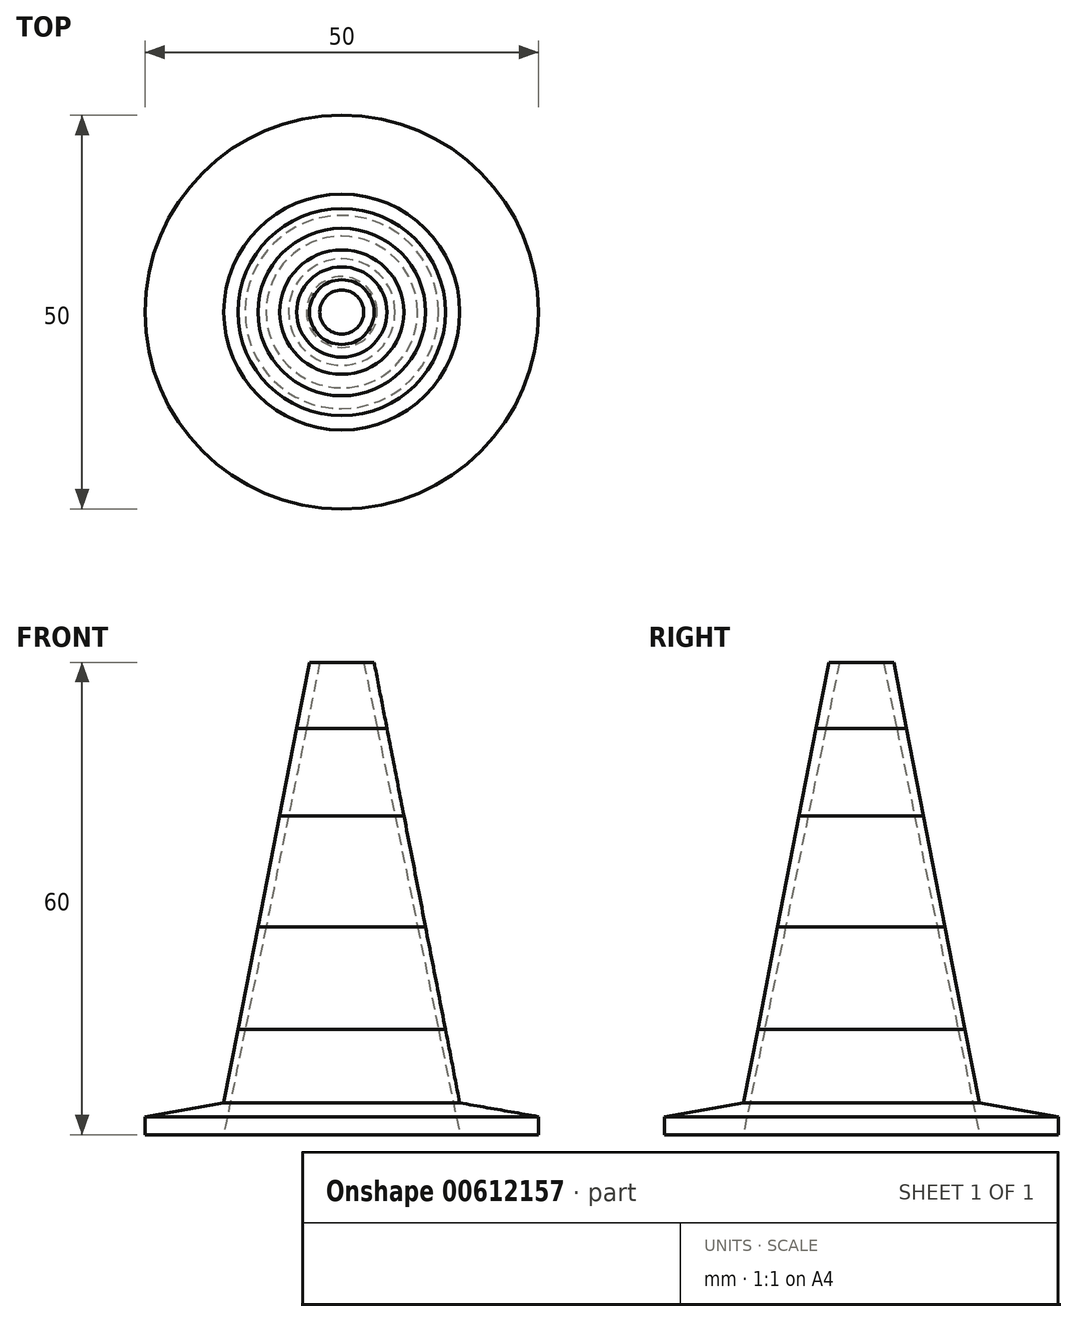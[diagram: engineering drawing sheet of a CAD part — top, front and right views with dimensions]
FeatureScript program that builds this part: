
annotation { "Feature Type Name" : "Feature", "Feature Type Description" : "" }
export const myFeature = defineFeature(function(context is Context, id is Id, definition is map)
    precondition{}
    {
        {
            var Q0;
            Q0=qCreatedBy(makeId("Front.planeOp"),FACE);
            var sketch = newSketch(context, id + "F0", { "sketchPlane" : qUnion([Q0])});
            skLineSegment(sketch, "E0", {"start": v(0, 0) * mm, "end": v(-25, 0) * mm});
            skLineSegment(sketch, "E1", {"start": v(-25, 0) * mm, "end": v(-25, 2.28) * mm});
            skLineSegment(sketch, "E2", {"start": v(-25, 2.28) * mm, "end": v(-14.98, 4.05) * mm});
            skLineSegment(sketch, "E3", {"start": v(-14.98, 4.05) * mm, "end": v(-4.1, 60) * mm});
            skLineSegment(sketch, "E4", {"start": v(-4.1, 60) * mm, "end": v(0, 60) * mm});
            skLineSegment(sketch, "E5", {"start": v(0, 60) * mm, "end": v(0, 0) * mm});
            skLineSegment(sketch, "E6", {"start": v(-13.17, 13.4) * mm, "end": v(0, 13.4) * mm});
            skLineSegment(sketch, "E7", {"start": v(-10.64, 26.4) * mm, "end": v(0, 26.4) * mm});
            skLineSegment(sketch, "E8", {"start": v(-7.9, 40.5) * mm, "end": v(0, 40.5) * mm});
            skLineSegment(sketch, "E9", {"start": v(-5.74, 51.6) * mm, "end": v(0, 51.6) * mm});
            skSolve(sketch);
        }
        {
            var Q0;
            {var subQ0=sQuery(id+"F0.wireOp",EDGE,"E4");Q0=makeQuery(id+"F0.imprint","IMPRINT",FACE,{"disambiguationData":[TD([[makeQuery(id+"F0.imprint","IMPRINT",EDGE,{"derivedFrom":subQ0}),-1.0]])]});}
            var Q1;
            Q1=sQuery(id+"F0.wireOp",EDGE,"E5");
            revolve(context, id + "F1", {"entities" : qUnion([Q0]), "axis" : qUnion([Q1]), "revolveType" : RevolveType.FULL});
        }
        {
            var Q0;
            {var subQ0=sQuery(id+"F0.wireOp",EDGE,"E8");Q0=makeQuery(id+"F0.imprint","IMPRINT",FACE,{"disambiguationData":[TD([[makeQuery(id+"F0.imprint","IMPRINT",EDGE,{"derivedFrom":subQ0}),1.0]])]});}
            var Q1;
            Q1=sQuery(id+"F0.wireOp",EDGE,"E5");
            revolve(context, id + "F2", {"entities" : qUnion([Q0]), "axis" : qUnion([Q1]), "revolveType" : RevolveType.FULL});
        }
        {
            var Q0;
            {var subQ0=sQuery(id+"F0.wireOp",EDGE,"E7");Q0=makeQuery(id+"F0.imprint","IMPRINT",FACE,{"disambiguationData":[TD([[makeQuery(id+"F0.imprint","IMPRINT",EDGE,{"derivedFrom":subQ0}),1.0]])]});}
            var Q1;
            Q1=sQuery(id+"F0.wireOp",EDGE,"E5");
            revolve(context, id + "F3", {"entities" : qUnion([Q0]), "axis" : qUnion([Q1]), "revolveType" : RevolveType.FULL});
        }
        {
            var Q0;
            {var subQ0=sQuery(id+"F0.wireOp",EDGE,"E6");Q0=makeQuery(id+"F0.imprint","IMPRINT",FACE,{"disambiguationData":[TD([[makeQuery(id+"F0.imprint","IMPRINT",EDGE,{"derivedFrom":subQ0}),1.0]])]});}
            var Q1;
            Q1=sQuery(id+"F0.wireOp",EDGE,"E5");
            revolve(context, id + "F4", {"entities" : qUnion([Q0]), "axis" : qUnion([Q1]), "revolveType" : RevolveType.FULL});
        }
        {
            var Q0;
            {var subQ4=sQuery(id+"F0.wireOp",EDGE,"E0");Q0=makeQuery(id+"F0.imprint","IMPRINT",FACE,{"disambiguationData":[TD([[makeQuery(id+"F0.imprint","IMPRINT",EDGE,{"derivedFrom":subQ4}),-1.0]])]});}
            var Q1;
            Q1=sQuery(id+"F0.wireOp",EDGE,"E5");
            revolve(context, id + "F5", {"entities" : qUnion([Q0]), "axis" : qUnion([Q1]), "revolveType" : RevolveType.FULL});
        }
        {
            var Q0;
            Q0=makeQuery(id+"F5.opRevolve","SWEPT_FACE",FACE,{"disambiguationData":[OSD([sQuery(id+"F0.wireOp",EDGE,"E0")])]});
            var sketch = newSketch(context, id + "F6", { "sketchPlane" : qUnion([Q0])});
            skCircle(sketch, "E10", {"center": v(0, 0) * mm, "radius": 15 * mm});
            skSolve(sketch);
        }
        {
            var Q0;
            Q0 = qSketchRegion(id + "F6", true);
            extrude(context, id + "F7", {"entities" : qUnion([Q0]), "operationType" : NewBodyOperationType.REMOVE, "endBound" : BoundingType.THROUGH_ALL, "oppositeDirection" : true, "depth" : 25 * mm, "offsetDistance" : 25 * mm, "hasDraft" : true, "draftAngle" : 11.5 * degree, "draftPullDirection" : true});
        }
    });
